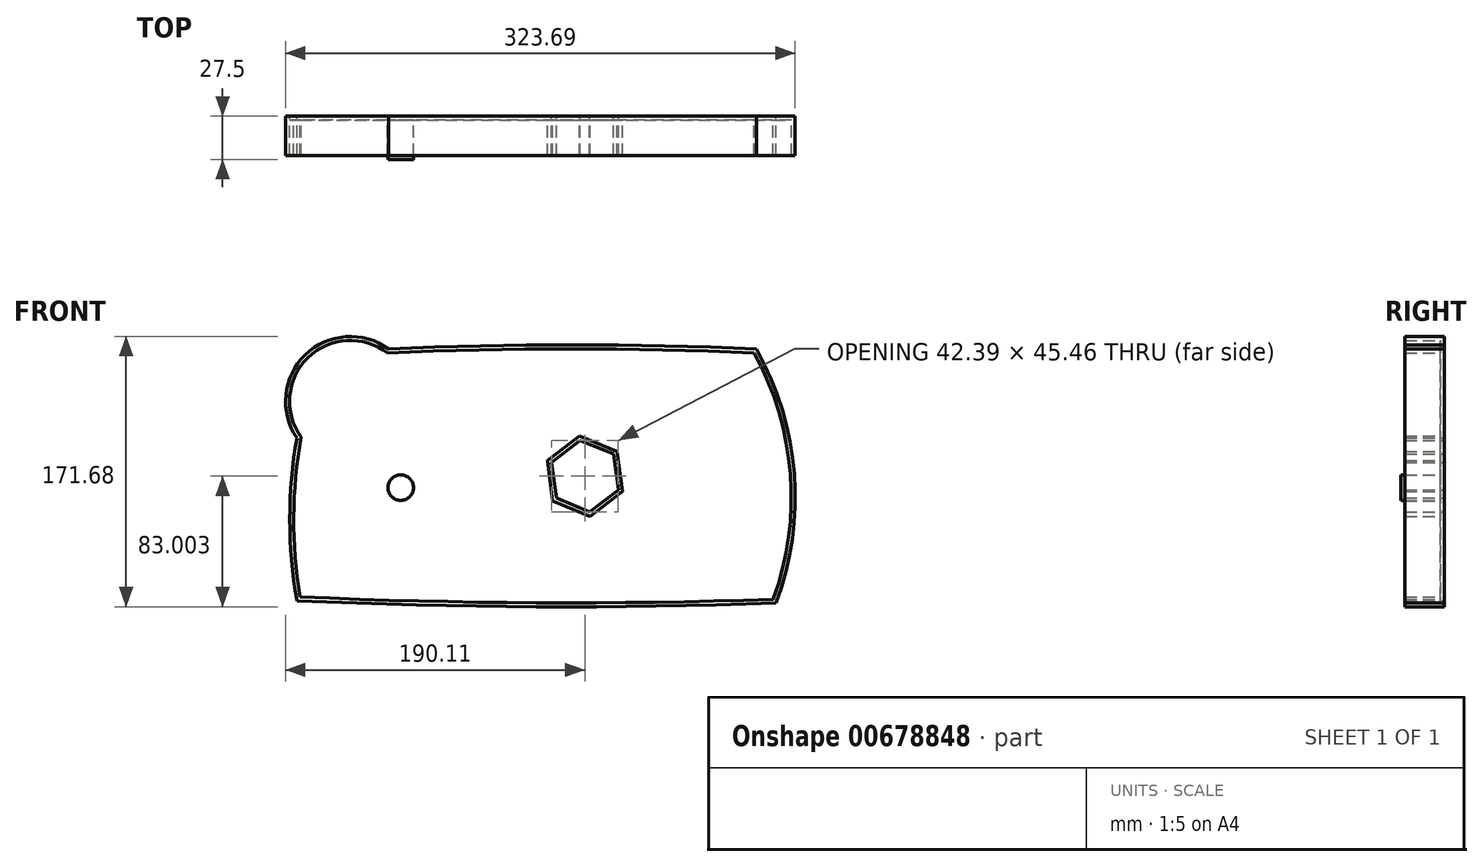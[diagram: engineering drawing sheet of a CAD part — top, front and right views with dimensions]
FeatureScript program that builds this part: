
annotation { "Feature Type Name" : "Feature", "Feature Type Description" : "" }
export const myFeature = defineFeature(function(context is Context, id is Id, definition is map)
    precondition{}
    {
        {
            var Q0;
            Q0=qCreatedBy(makeId("Front.planeOp"),FACE);
            var sketch = newSketch(context, id + "F0", { "sketchPlane" : qUnion([Q0])});
            skArc(sketch, "E0", {"start": v(201.52, -108.22) * mm, "mid": v(213.16, -26.14) * mm, "end": v(189, 53.16) * mm});
            skArc(sketch, "E1", {"start": v(189, 53.16) * mm, "mid": v(72.26, 55.8) * mm, "end": v(-44.48, 53.16) * mm});
            skArc(sketch, "E2", {"start": v(-44.48, 53.16) * mm, "mid": v(-97.43, 49.54) * mm, "end": v(-102.78, -3.27) * mm});
            skArc(sketch, "E3", {"start": v(-102.78, -3.27) * mm, "mid": v(-107.29, -54.97) * mm, "end": v(-102.78, -106.67) * mm});
            skArc(sketch, "E4", {"start": v(-102.78, -106.67) * mm, "mid": v(49.36, -110.5) * mm, "end": v(201.52, -108.22) * mm});
            skCircle(sketch, "E5", {"center": v(79.43, -27.71) * mm, "radius": 9.6 * mm});
            skLineSegment(sketch, "E6.0", {"start": v(77.13, -4.83) * mm, "end": v(98.32, -13.57) * mm});
            skLineSegment(sketch, "E6.1", {"start": v(98.32, -13.57) * mm, "end": v(101.35, -36.3) * mm});
            skLineSegment(sketch, "E6.2", {"start": v(101.35, -36.3) * mm, "end": v(83.17, -50.29) * mm});
            skLineSegment(sketch, "E6.3", {"start": v(83.17, -50.29) * mm, "end": v(61.98, -41.54) * mm});
            skLineSegment(sketch, "E6.4", {"start": v(61.98, -41.54) * mm, "end": v(58.95, -18.8) * mm});
            skLineSegment(sketch, "E6.5", {"start": v(58.95, -18.8) * mm, "end": v(77.13, -4.83) * mm});
            skSolve(sketch);
        }
        {
            var Q0;
            Q0=makeQuery(id+"F0.imprint","IMPRINT",FACE,{"disambiguationData":[TD([[makeQuery(id+"F0.imprint","IMPRINT",EDGE,{"derivedFrom":sQuery(id+"F0.wireOp",EDGE,"E0")}),1.0]])]});
            extrude(context, id + "F1", {"entities" : qUnion([Q0]), "depth" : 25 * mm, "offsetDistance" : 25 * mm});
        }
        {
            var Q0;
            Q0=makeQuery(id+"F1.opExtrude","CAP_FACE",FACE,{"disambiguationData":[OSD([sQuery(id+"F0.wireOp",EDGE,"E0"),sQuery(id+"F0.wireOp",EDGE,"E1"),sQuery(id+"F0.wireOp",EDGE,"E2"),sQuery(id+"F0.wireOp",EDGE,"E3"),sQuery(id+"F0.wireOp",EDGE,"E4")])],"isStart":false});
            shell(context, id + "F2", {"entities" : qUnion([Q0]), "thickness" : 2.5 * mm});
        }
        {
            var Q0;
            {var subQ0=sQuery(id+"F0.wireOp",EDGE,"QRxqCNhj-ZsV3-sHRW-dGer-QxIwV9FeGUns");var subQ1=sQuery(id+"F0.wireOp",EDGE,"bUynxPdC-4oAV-4umz-r0zd-eGPOrQgAVA4F");var subQ2=sQuery(id+"F0.wireOp",EDGE,"E4");var subQ3=sQuery(id+"F0.wireOp",EDGE,"E3");var subQ4=sQuery(id+"F0.wireOp",EDGE,"E2");var subQ5=sQuery(id+"F0.wireOp",EDGE,"E1");var subQ6=sQuery(id+"F0.wireOp",EDGE,"E0");Q0=makeQuery(id+"F2.opShell","OFFSET_FACE",FACE,{"disambiguationData":[OSD([subQ6,subQ5,subQ4,subQ3,subQ2,subQ1,subQ0]),TDD([makeQuery(id+"F1.opExtrude","CAP_FACE",FACE,{"disambiguationData":[OSD([subQ6,subQ5,subQ4,subQ3,subQ2,subQ1,subQ0])],"isStart":true})])]});}
            var sketch = newSketch(context, id + "F3", { "sketchPlane" : qUnion([Q0])});
            skCircle(sketch, "E7", {"center": v(-36.8, -34.88) * mm, "radius": 8.07 * mm});
            skSolve(sketch);
        }
        {
            var Q0;
            Q0=makeQuery(id+"F3.imprint","IMPRINT",FACE,{"disambiguationData":[TD([[makeQuery(id+"F3.imprint","IMPRINT",EDGE,{"derivedFrom":sQuery(id+"F3.wireOp",EDGE,"E7")}),1.0]])]});
            extrude(context, id + "F4", {"entities" : qUnion([Q0]), "operationType" : NewBodyOperationType.ADD, "depth" : 25 * mm, "offsetDistance" : 25 * mm});
        }
    });
